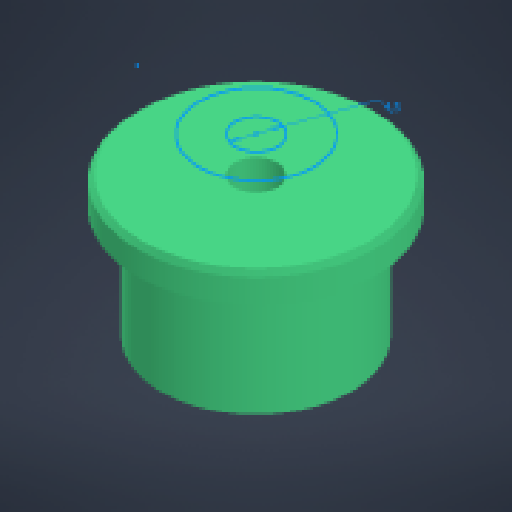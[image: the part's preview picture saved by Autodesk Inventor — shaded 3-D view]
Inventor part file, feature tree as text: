
AUTODESK INVENTOR PART (.ipt)
format: ipt  version: 2024 (Build 280153000, 153)  size: 164,864 bytes
history: native  units: mm
features: other x8, extrude x4, sketch x4, reference x2, chamfer x1
ambient origin geometry x8: Origin, YZ Plane, XZ Plane, XY Plane, X Axis, Y Axis, Z Axis, Center Point
bodies: Body1 (feature_tree)
feature tree (19):
  other  "Твердое тело1"
  other  "РабПлоскость1"
  extrude  "Выдавливание1"  Depth=11.75mm TaperAngle=0.0deg
  extrude  "Выдавливание2"  Depth=3.0mm TaperAngle=0.0deg
  chamfer  "Фаска1"  Distance=0.5mm Angle=45.0deg
  extrude  "Выдавливание8"  Depth=12.0mm
  extrude  "Выдавливание9"  Depth=5.0mm TaperAngle=0.0deg
  other  "РабПлоскость3"
  sketch  "Эскиз1"
  reference  "Ссылка1"
  sketch  "Эскиз2"
  reference  "Ссылка2"
  sketch  "Эскиз8"
  sketch  "Эскиз9"
  parser-record x2  (decoder bookkeeping rows leaked as tree rows — omitted from the tree; the rows remain in map.json)
  other  "motor_assembly_S.iam"
  other  "lower_arm:1"
  other  "motor_assembly.iam"
note: 2 file-system paths scrubbed to <path> (originals preserved in map.json)
